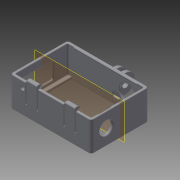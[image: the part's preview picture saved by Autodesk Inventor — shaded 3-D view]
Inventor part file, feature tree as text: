
AUTODESK INVENTOR PART (.ipt)
format: ipt  version: 2015 (Build 190159000, 159)  size: 651,776 bytes
history: native  units: mm
features: fillet x25, sketch x12, extrude x10, hole x5, plane x2, mirror x2
ambient origin geometry x8: Origin, YZ Plane, XZ Plane, XY Plane, X Axis, Y Axis, Z Axis, Center Point
bodies: Solid1 (feature_tree)
feature tree (56):
  sketch  "Sketch1"  dims[d0=60.0mm d1=41.5mm]
  extrude  "Extrusion1"  Depth=41.5mm
  extrude  "Extrusion2"  Depth=3.0mm
  extrude  "Extrusion3"  Depth=2.0mm TaperAngle=0.0deg
  plane  "Work Plane1"
  mirror  "Mirror1"
  extrude  "Extrusion4"  Depth=20.0mm
  extrude  "Extrusion5"  Depth=15.0mm
  mirror  "Mirror2"
  fillet  "Fillet5"  [1 undecoded]
  fillet  "Fillet6"  Radius=1.0mm
  fillet  "Fillet7"  Radius=8.0mm
  extrude  "Extrusion6"  Depth=23.5mm TaperAngle=0.0deg
  fillet  "Fillet8"  Radius=2.0mm
  sketch  "Sketch6"  dims[d19=1.0mm d20=23.5mm d21=0.0mm d22=2.0mm d23=0.0mm]
  hole  "Hole1"  [1 undecoded]
  fillet  "Fillet9"  Radius=2.0mm
  fillet  "Fillet10"  Radius=0.5mm
  hole  "Hole2"  [1 undecoded]
  fillet  "Fillet11"  Radius=50.0mm
  extrude  "Extrusion7"  Depth=0.5mm
  fillet  "Fillet13"  Radius=15.0mm
  fillet  "Fillet14"  Radius=12.5mm
  hole  "Hole3"  [1 undecoded]
  fillet  "Fillet15"  Radius=0.5mm
  fillet  "Fillet16"  Radius=7.0mm
  extrude  "Extrusion8"  Depth=0.5mm
  fillet  "Fillet17"  Radius=24.0mm
  hole  "Hole4"  [1 undecoded]
  fillet  "Fillet18"  Radius=2.0mm
  extrude  "Extrusion9"  Depth=0.5mm
  fillet  "Fillet19"  Radius=4.0mm
  fillet  "Fillet20"  Radius=1.0mm
  fillet  "Fillet21"  Radius=1.0mm
  fillet  "Fillet22"  Radius=0.5mm
  fillet  "Fillet24"  Radius=12.0mm
  fillet  "Fillet25"  Radius=12.0mm
  fillet  "Fillet29"  Radius=1.0mm
  plane  "Work Plane2"
  extrude  "Extrusion11"  Depth=0.5mm
  fillet  "Fillet33"  Radius=0.5mm
  fillet  "Fillet34"  Radius=0.5mm
  hole  "Hole6"  [1 undecoded]
  fillet  "Fillet35"  Radius=9.5mm
  fillet  "Fillet36"  Radius=0.5mm
  fillet  "Fillet37"  Radius=4.0mm
  sketch  "Sketch2"  dims[d2=2.0mm d3=3.0mm]
  sketch  "Sketch3"  dims[d4=3.0mm d5=2.0mm d6=0.0mm]
  sketch  "Sketch4"  dims[d7=23.5mm d8=0.0mm d13=20.0mm]
  sketch  "Sketch5"  dims[d14=20.0mm d15=15.0mm d16=90.0deg d17=1.0mm d18=8.0mm]
  sketch  "Sketch7"  dims[d24=2.0mm d25=0.0mm d30=1.0mm d31=2.0mm d32=0.5mm]
  sketch  "Sketch8"  dims[d34=25.0mm d36=1.0mm d37=50.0mm]
  sketch  "Sketch9"  dims[d38=0.5mm d39=0.0mm d40=0.5mm d41=15.0mm d42=12.5mm]
  sketch  "Sketch10"  dims[d43=13.0mm d44=6.0mm d45=4.0mm d46=2.0mm d47=90.0deg d48=2.0mm d49=20.594885mm d50=1.0mm d51=0.5mm d52=7.0mm]
  sketch  "Sketch14"  dims[d53=7.5mm]
  sketch  "Sketch15"  dims[d54=2.5mm d55=6.0mm d56=4.0mm d57=2.0mm d58=90.0deg d59=2.0mm d60=20.594885mm d61=0.5mm d64=24.0mm d65=2.5mm d66=2.0mm d67=5.0mm d68=4.0mm d69=1.0mm d70=0.0mm d71=1.0mm d72=0.5mm d73=12.0mm d74=12.0mm d75=10.0mm d76=6.0mm d77=4.0mm d78=2.0mm d79=90.0deg d80=2.0mm d81=20.594885mm d82=1.0mm d83=0.5mm d84=0.5mm d85=0.0mm d86=0.5mm d87=5.0mm d88=9.5mm d89=3.0mm d90=6.0mm d91=4.0mm d92=2.0mm d93=90.0deg d94=2.0mm d95=20.594885mm d96=0.5mm d97=4.0mm d98=7.0mm d99=13.0mm d100=25.0mm d101=2.0mm d102=0.0mm d103=1.0mm d104=1.0mm d105=1.0mm d106=2.0mm d108=0.5mm d109=0.5mm d131=0.5mm d137=3.3mm d138=3.0mm d139=3.0mm d140=15.0mm d141=16.5mm d142=0.0mm d143=7.0mm d144=7.5mm d145=5.5mm d146=5.5mm d147=6.0mm d148=4.0mm d149=2.0mm d150=90.0deg d151=8.0mm d152=20.594885mm d153=0.5mm d154=0.5mm d155=0.5mm]
note: 6 required parameter values undecoded (feature->parameter linkage not recoverable at this tier; creation-order binding heuristic only, values carry confidence <= 0.55)
